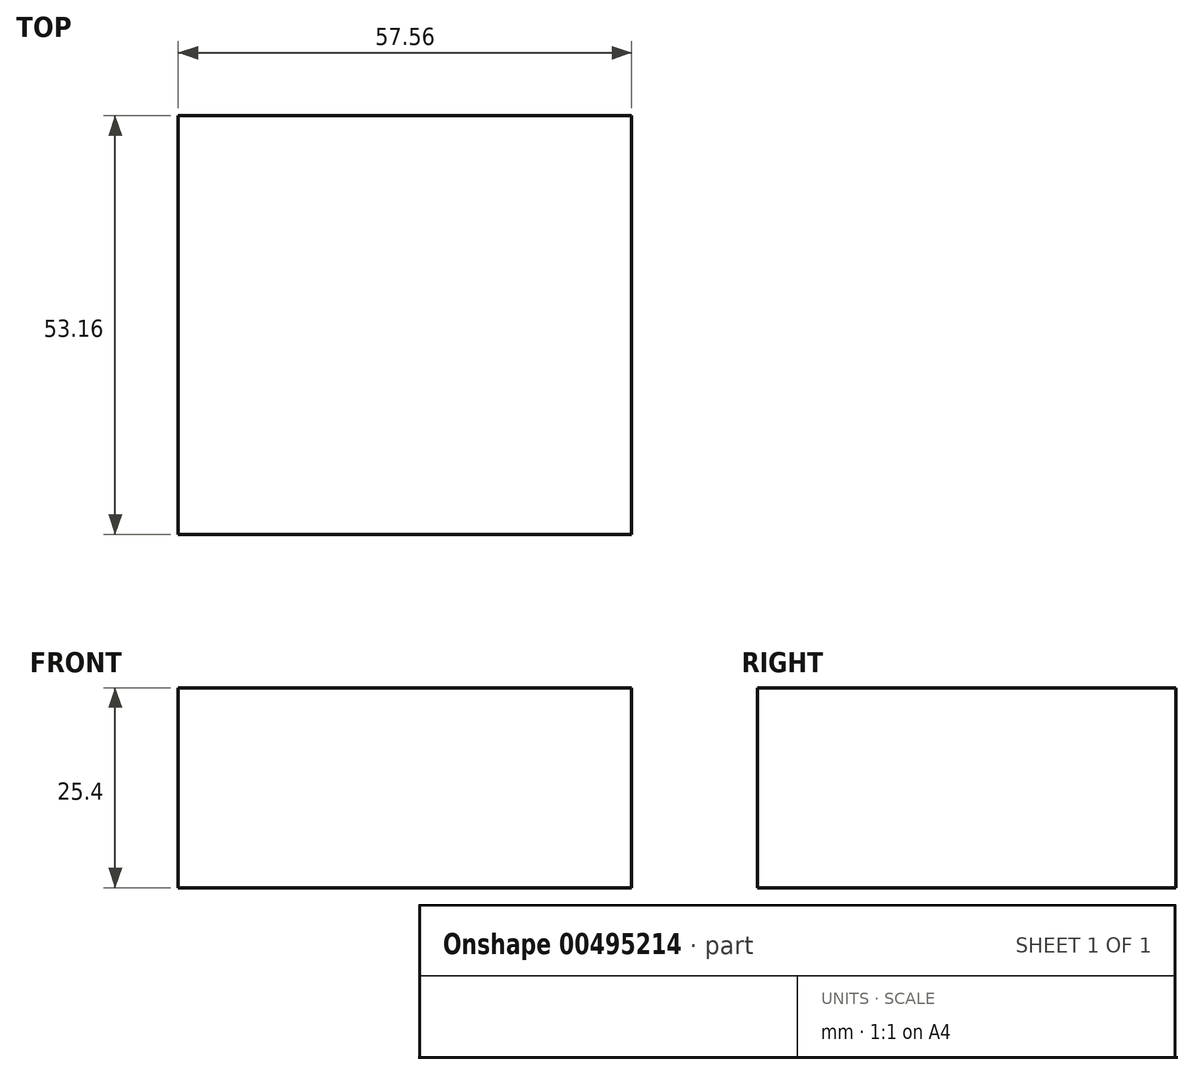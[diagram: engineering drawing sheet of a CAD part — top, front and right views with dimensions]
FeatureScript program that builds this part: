
annotation { "Feature Type Name" : "Feature", "Feature Type Description" : "" }
export const myFeature = defineFeature(function(context is Context, id is Id, definition is map)
    precondition{}
    {
        {
            var Q0;
            Q0=qCreatedBy(makeId("Top.planeOp"),FACE);
            var sketch = newSketch(context, id + "F0", { "sketchPlane" : qUnion([Q0])});
            skLineSegment(sketch, "E0.bottom", {"start": v(0, 0) * mm, "end": v(57.56, 0) * mm});
            skLineSegment(sketch, "E0.top", {"start": v(0, 53.16) * mm, "end": v(57.56, 53.16) * mm});
            skLineSegment(sketch, "E0.left", {"start": v(0, 0) * mm, "end": v(0, 53.16) * mm});
            skLineSegment(sketch, "E0.right", {"start": v(57.56, 0) * mm, "end": v(57.56, 53.16) * mm});
            skSolve(sketch);
        }
        {
            var Q0;
            Q0=makeQuery(id+"F0.imprint","IMPRINT",FACE,{"disambiguationData":[TD([[makeQuery(id+"F0.imprint","IMPRINT",EDGE,{"derivedFrom":sQuery(id+"F0.wireOp",EDGE,"E0.bottom")}),1.0]])]});
            extrude(context, id + "F1", {"entities" : qUnion([Q0]), "depth" : 25.4 * mm});
        }
    });
